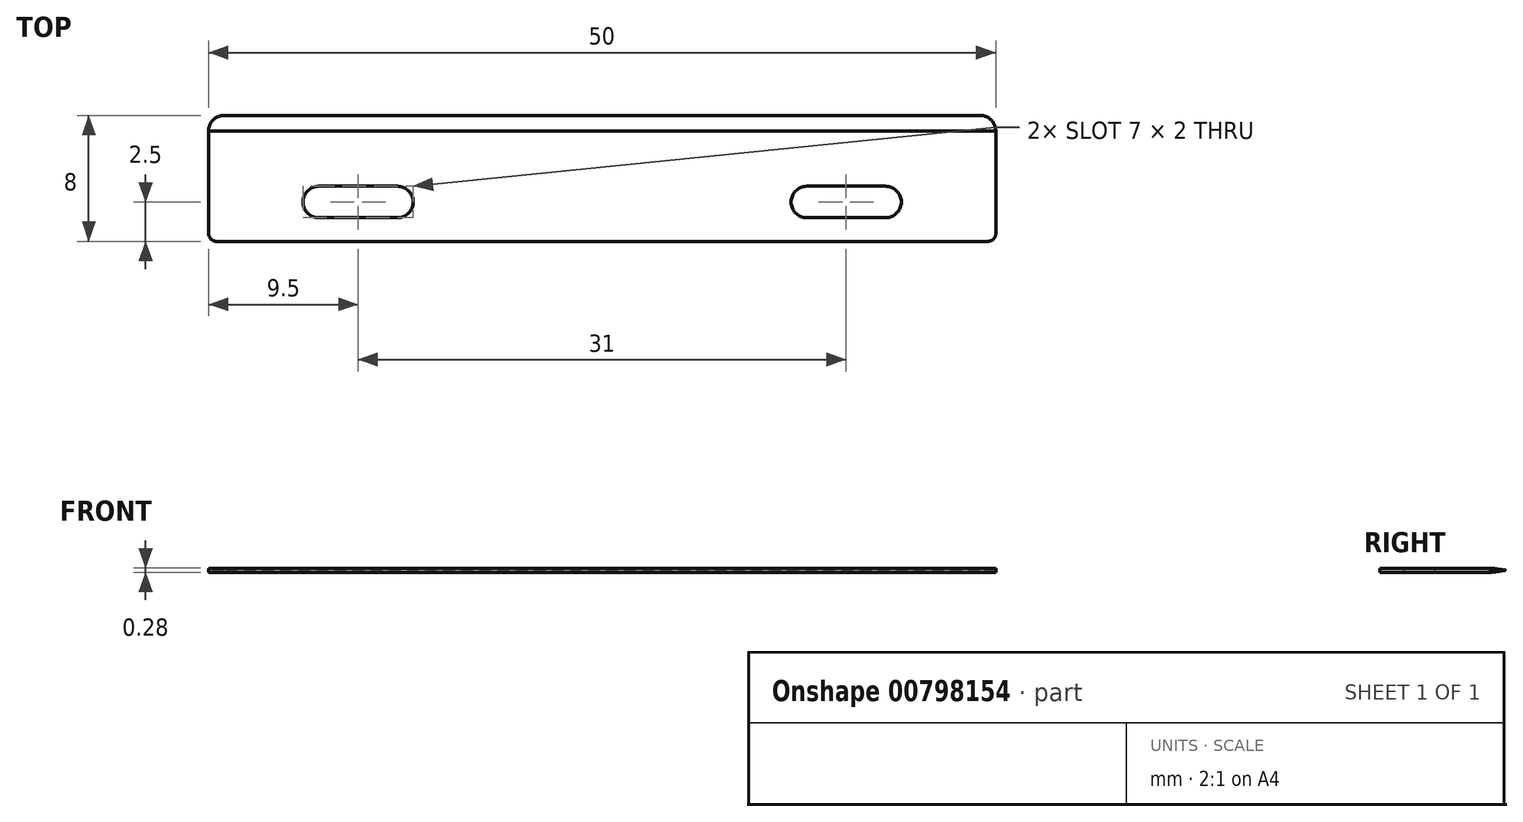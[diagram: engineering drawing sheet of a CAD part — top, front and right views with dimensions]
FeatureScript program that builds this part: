
annotation { "Feature Type Name" : "Feature", "Feature Type Description" : "" }
export const myFeature = defineFeature(function(context is Context, id is Id, definition is map)
    precondition{}
    {
        {
            var Q0;
            Q0=qCreatedBy(makeId("Top.planeOp"),FACE);
            var sketch = newSketch(context, id + "F0", { "sketchPlane" : qUnion([Q0])});
            skLineSegment(sketch, "E0", {"start": v(0, 0) * mm, "end": v(24.5, 0) * mm});
            skLineSegment(sketch, "E1", {"start": v(25, 0.5) * mm, "end": v(25, 7) * mm});
            skLineSegment(sketch, "E2", {"start": v(24, 8) * mm, "end": v(0, 8) * mm});
            skPoint(sketch, "E3.visualSharp", {"position": v(25, 8) * mm});
            skArc(sketch, "E3.filletArc", {"start": v(25, 7) * mm, "mid": v(24.7, 7.7) * mm, "end": v(24, 8) * mm});
            skLineSegment(sketch, "E4", {"start": v(25, 7) * mm, "end": v(0, 7) * mm});
            skLineSegment(sketch, "E5", {"start": v(0, 8) * mm, "end": v(0, 0) * mm, "construction": true});
            skLineSegment(sketch, "E6.MirrorCS", {"start": v(-25, 7) * mm, "end": v(0, 7) * mm});
            skArc(sketch, "E7.MirrorCS", {"start": v(-25, 7) * mm, "mid": v(-24.7, 7.7) * mm, "end": v(-24, 8) * mm});
            skPoint(sketch, "E8.MirrorP", {"position": v(-25, 8) * mm});
            skLineSegment(sketch, "E9.MirrorCS", {"start": v(0, 0) * mm, "end": v(-24.5, 0) * mm});
            skLineSegment(sketch, "E10.MirrorCS", {"start": v(-24, 8) * mm, "end": v(0, 8) * mm});
            skLineSegment(sketch, "E11.MirrorCS", {"start": v(-25, 0.5) * mm, "end": v(-25, 7) * mm});
            skPoint(sketch, "E12.visualSharp", {"position": v(25, 0) * mm});
            skArc(sketch, "E12.filletArc", {"start": v(24.5, 0) * mm, "mid": v(24.85, 0.15) * mm, "end": v(25, 0.5) * mm});
            skPoint(sketch, "E13.visualSharp", {"position": v(-25, 0) * mm});
            skArc(sketch, "E13.filletArc", {"start": v(-25, 0.5) * mm, "mid": v(-24.85, 0.15) * mm, "end": v(-24.5, 0) * mm});
            skLineSegment(sketch, "E14", {"start": v(-25, 0) * mm, "end": v(-25, 1.5) * mm, "construction": true});
            skLineSegment(sketch, "E15", {"start": v(-25, 1.5) * mm, "end": v(25, 1.5) * mm, "construction": true});
            skLineSegment(sketch, "E16", {"start": v(-25, 8) * mm, "end": v(-25, 3.5) * mm, "construction": true});
            skLineSegment(sketch, "E17", {"start": v(-25, 3.5) * mm, "end": v(25, 3.5) * mm, "construction": true});
            skLineSegment(sketch, "E18", {"start": v(25, 0) * mm, "end": v(25, 8) * mm, "construction": true});
            skLineSegment(sketch, "E19", {"start": v(-25, 2.5) * mm, "end": v(-19, 2.5) * mm, "construction": true});
            skLineSegment(sketch, "E20", {"start": v(-25, 1.5) * mm, "end": v(-25, 3.5) * mm, "construction": true});
            skCircle(sketch, "E21", {"center": v(-18, 2.5) * mm, "radius": 1 * mm});
            skLineSegment(sketch, "E22", {"start": v(-19, 2.5) * mm, "end": v(-12, 2.5) * mm, "construction": true});
            skCircle(sketch, "E23", {"center": v(-13, 2.5) * mm, "radius": 1 * mm});
            skLineSegment(sketch, "E24", {"start": v(-18, 3.5) * mm, "end": v(-13, 3.5) * mm});
            skLineSegment(sketch, "E25", {"start": v(-13, 3.5) * mm, "end": v(-13, 1.5) * mm});
            skLineSegment(sketch, "E26", {"start": v(-13, 1.5) * mm, "end": v(-18, 1.5) * mm});
            skLineSegment(sketch, "E27", {"start": v(-18, 1.5) * mm, "end": v(-18, 3.5) * mm});
            skArc(sketch, "E28.MirrorCS", {"start": v(25, 0.5) * mm, "mid": v(24.85, 0.15) * mm, "end": v(24.5, 0) * mm});
            skLineSegment(sketch, "E29.MirrorCS", {"start": v(13, 1.5) * mm, "end": v(18, 1.5) * mm});
            skLineSegment(sketch, "E30.MirrorCS", {"start": v(18, 1.5) * mm, "end": v(18, 3.5) * mm});
            skLineSegment(sketch, "E31.MirrorCS", {"start": v(25, 2.5) * mm, "end": v(19, 2.5) * mm, "construction": true});
            skCircle(sketch, "E32.MirrorC", {"center": v(13, 2.5) * mm, "radius": 1 * mm});
            skLineSegment(sketch, "E33.MirrorCS", {"start": v(19, 2.5) * mm, "end": v(12, 2.5) * mm, "construction": true});
            skLineSegment(sketch, "E34.MirrorCS", {"start": v(18, 3.5) * mm, "end": v(13, 3.5) * mm});
            skLineSegment(sketch, "E35.MirrorCS", {"start": v(25, 0) * mm, "end": v(25, 1.5) * mm, "construction": true});
            skLineSegment(sketch, "E36.MirrorCS", {"start": v(25, 1.5) * mm, "end": v(25, 3.5) * mm, "construction": true});
            skCircle(sketch, "E37.MirrorC", {"center": v(18, 2.5) * mm, "radius": 1 * mm});
            skLineSegment(sketch, "E38.MirrorCS", {"start": v(13, 3.5) * mm, "end": v(13, 1.5) * mm});
            skSolve(sketch);
        }
        {
            var Q0;
            Q0=makeQuery(id+"F0.imprint","IMPRINT",FACE,{"disambiguationData":[TD([[makeQuery(id+"F0.imprint","IMPRINT",EDGE,{"derivedFrom":sQuery(id+"F0.wireOp",EDGE,"E0")}),1.0]])]});
            extrude(context, id + "F1", {"entities" : qUnion([Q0]), "endBound" : BoundingType.SYMMETRIC, "depth" : 0.25 * mm, "offsetDistance" : 25 * mm});
        }
        {
            var Q0;
            Q0=makeQuery(id+"F0.imprint","IMPRINT",FACE,{"disambiguationData":[TD([[makeQuery(id+"F0.imprint","IMPRINT",EDGE,{"derivedFrom":sQuery(id+"F0.wireOp",EDGE,"E2")}),1.0]])]});
            var Q1;
            Q1=sQuery(id+"F0.wireOp",EDGE,"E2");
            revolve(context, id + "F2", {"operationType" : NewBodyOperationType.ADD, "surfaceOperationType" : NewSurfaceOperationType.NEW, "entities" : qUnion([Q0]), "axis" : qUnion([Q1]), "revolveType" : RevolveType.SYMMETRIC, "oppositeDirection" : true, "angle" : 16 * degree});
        }
    });
